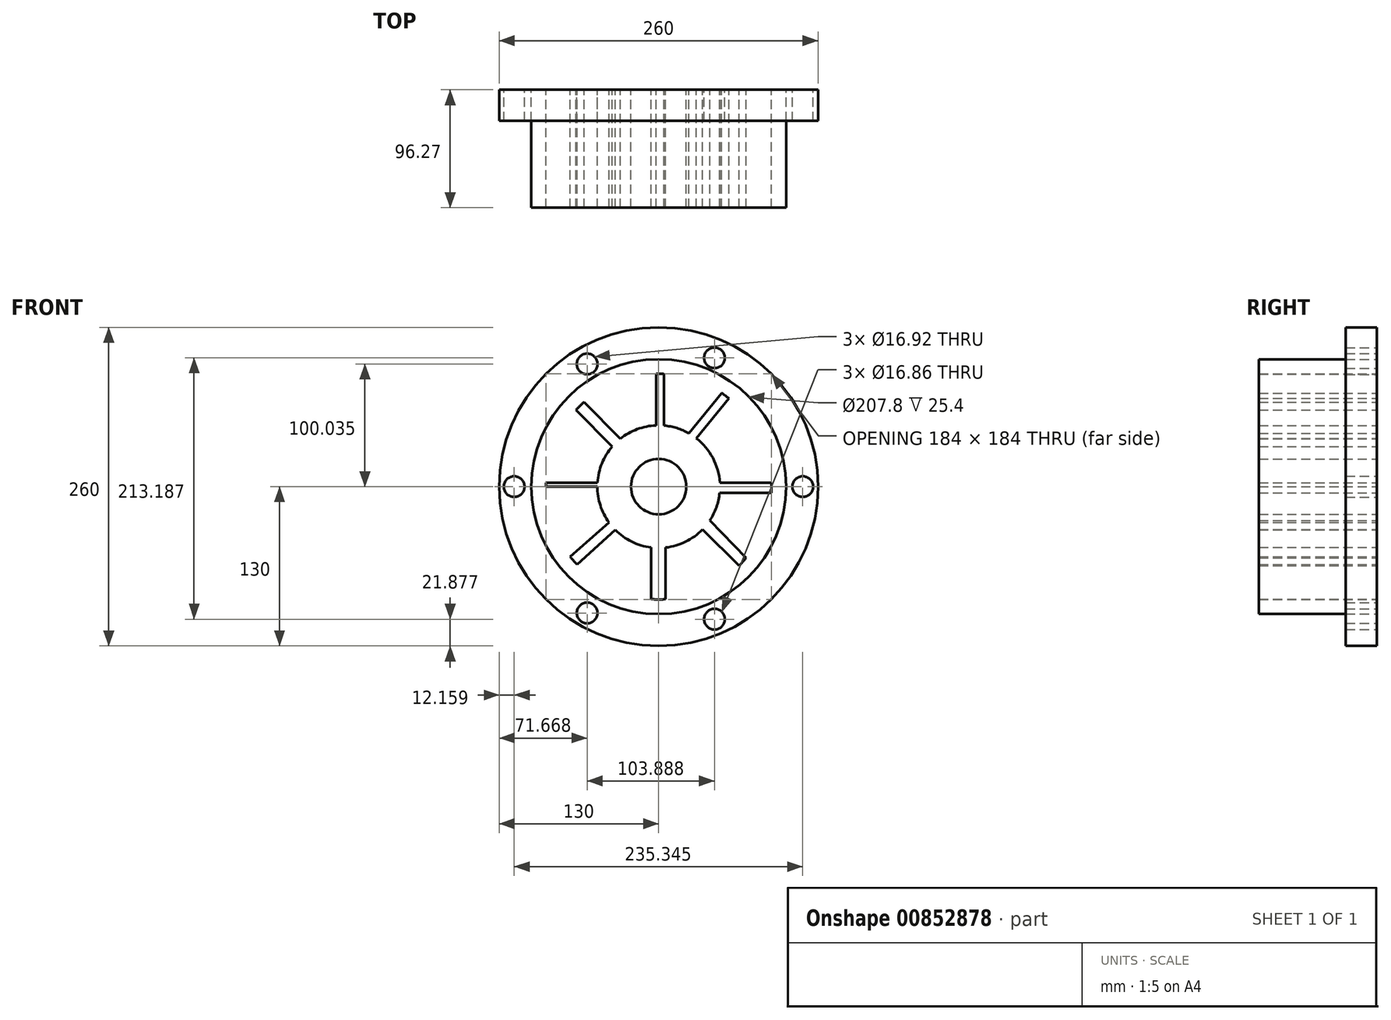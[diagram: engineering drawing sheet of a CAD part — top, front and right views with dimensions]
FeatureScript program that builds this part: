
annotation { "Feature Type Name" : "Feature", "Feature Type Description" : "" }
export const myFeature = defineFeature(function(context is Context, id is Id, definition is map)
    precondition{}
    {
        {
            var Q0;
            Q0=qCreatedBy(makeId("Front.planeOp"),FACE);
            var sketch = newSketch(context, id + "F0", { "sketchPlane" : qUnion([Q0])});
            skCircle(sketch, "E0", {"center": v(0, 0) * mm, "radius": 40 * mm});
            skCircle(sketch, "E1", {"center": v(0, 0) * mm, "radius": 22.57 * mm});
            skCircle(sketch, "E2", {"center": v(0, 0) * mm, "radius": 45 * mm});
            skCircle(sketch, "E3", {"center": v(0, 0) * mm, "radius": 50 * mm});
            skCircle(sketch, "E4", {"center": v(0, 0) * mm, "radius": 103.9 * mm});
            skCircle(sketch, "E5", {"center": v(0, 0) * mm, "radius": 92 * mm});
            skCircle(sketch, "E6", {"center": v(0, 0) * mm, "radius": 100 * mm});
            skCircle(sketch, "E7", {"center": v(0, 0) * mm, "radius": 130 * mm});
            skCircle(sketch, "E8", {"center": v(-117.84, 0) * mm, "radius": 8.46 * mm});
            skCircle(sketch, "E9", {"center": v(117.5, 0) * mm, "radius": 8.46 * mm});
            skCircle(sketch, "E10", {"center": v(-58.33, 100.04) * mm, "radius": 8.46 * mm});
            skCircle(sketch, "E11", {"center": v(45.56, 105.06) * mm, "radius": 8.43 * mm});
            skCircle(sketch, "E12", {"center": v(-58.33, -103.05) * mm, "radius": 8.43 * mm});
            skCircle(sketch, "E13", {"center": v(45.56, -108.12) * mm, "radius": 8.43 * mm});
            skLineSegment(sketch, "E14", {"start": v(2.97, -49.91) * mm, "end": v(2.97, -91.95) * mm});
            skLineSegment(sketch, "E15", {"start": v(-4.36, -49.8) * mm, "end": v(-4.36, -91.9) * mm});
            skLineSegment(sketch, "E16", {"start": v(-6.18, -49.62) * mm, "end": v(-6.18, -91.8) * mm});
            skLineSegment(sketch, "E17", {"start": v(5.65, -49.68) * mm, "end": v(5.65, -91.83) * mm});
            skLineSegment(sketch, "E18", {"start": v(-36.4, -34.28) * mm, "end": v(-67.47, -62.54) * mm});
            skLineSegment(sketch, "E19", {"start": v(-71.39, -58.03) * mm, "end": v(-39.83, -30.23) * mm});
            skLineSegment(sketch, "E20", {"start": v(-40.57, -29.23) * mm, "end": v(-72.16, -57.07) * mm});
            skLineSegment(sketch, "E21", {"start": v(-66.45, -63.62) * mm, "end": v(-35.36, -35.35) * mm});
            skLineSegment(sketch, "E22", {"start": v(-49.98, 1.43) * mm, "end": v(-91.99, 1.43) * mm});
            skLineSegment(sketch, "E23", {"start": v(-50, 0) * mm, "end": v(-92, 0) * mm});
            skLineSegment(sketch, "E24", {"start": v(-91.99, -1.6) * mm, "end": v(-50, -1.6) * mm});
            skLineSegment(sketch, "E25", {"start": v(-91.94, 3.26) * mm, "end": v(-49.9, 3.26) * mm});
            skLineSegment(sketch, "E26.MirrorCS", {"start": v(-91.99, 1.6) * mm, "end": v(-50, 1.6) * mm});
            skLineSegment(sketch, "E27", {"start": v(2.03, 49.96) * mm, "end": v(2.03, 91.98) * mm});
            skLineSegment(sketch, "E28", {"start": v(0, 92) * mm, "end": v(0, 49.96) * mm});
            skLineSegment(sketch, "E29", {"start": v(-2.07, 91.98) * mm, "end": v(-2.07, 49.96) * mm});
            skLineSegment(sketch, "E30", {"start": v(4.32, 91.9) * mm, "end": v(4.32, 49.81) * mm});
            skLineSegment(sketch, "E31", {"start": v(28.76, 40.9) * mm, "end": v(55.54, 73.34) * mm});
            skLineSegment(sketch, "E32", {"start": v(53.79, 74.64) * mm, "end": v(27.07, 42.04) * mm});
            skLineSegment(sketch, "E33", {"start": v(57.35, 71.94) * mm, "end": v(30.72, 39.45) * mm});
            skLineSegment(sketch, "E34", {"start": v(51.4, 76.3) * mm, "end": v(24.55, 43.56) * mm});
            skLineSegment(sketch, "E35", {"start": v(-33.6, 37.03) * mm, "end": v(-63.15, 66.9) * mm});
            skLineSegment(sketch, "E36", {"start": v(-65.36, 64.75) * mm, "end": v(-35.65, 35.06) * mm});
            skLineSegment(sketch, "E37", {"start": v(-67.54, 62.47) * mm, "end": v(-37.79, 32.74) * mm});
            skLineSegment(sketch, "E38", {"start": v(-60.8, 69.04) * mm, "end": v(-31.18, 39.1) * mm});
            skLineSegment(sketch, "E39", {"start": v(50, 0) * mm, "end": v(92, 0) * mm});
            skLineSegment(sketch, "E40", {"start": v(49.96, -2) * mm, "end": v(91.98, -2) * mm});
            skLineSegment(sketch, "E41", {"start": v(49.9, 3.22) * mm, "end": v(91.94, 3.22) * mm});
            skLineSegment(sketch, "E42", {"start": v(49.74, -5.08) * mm, "end": v(91.86, -5.08) * mm});
            skLineSegment(sketch, "E43", {"start": v(37.83, -32.7) * mm, "end": v(67.58, -62.42) * mm});
            skLineSegment(sketch, "E44", {"start": v(39.6, -30.54) * mm, "end": v(69.39, -60.4) * mm});
            skLineSegment(sketch, "E45", {"start": v(41.7, -27.58) * mm, "end": v(71.39, -58.03) * mm});
            skLineSegment(sketch, "E46", {"start": v(35.79, -34.92) * mm, "end": v(65.6, -64.5) * mm});
            skSolve(sketch);
        }
        {
            var Q0;
            Q0=makeQuery(id+"F0.imprint","IMPRINT",FACE,{"disambiguationData":[TD([[makeQuery(id+"F0.imprint","IMPRINT",EDGE,{"derivedFrom":sQuery(id+"F0.wireOp",EDGE,"E4")}),-1.0]])]});
            extrude(context, id + "F1", {"entities" : qUnion([Q0]), "depth" : 25.4 * mm, "offsetDistance" : 25.4 * mm});
        }
        {
            var Q0;
            Q0=makeQuery(id+"F0.imprint","IMPRINT",FACE,{"disambiguationData":[TD([[makeQuery(id+"F0.imprint","IMPRINT",EDGE,{"derivedFrom":sQuery(id+"F0.wireOp",EDGE,"E1")}),1.0]])]});
            var Q1;
            {var subQ0=sQuery(id+"F0.wireOp",EDGE,"E29");Q1=makeQuery(id+"F0.imprint","IMPRINT",FACE,{"disambiguationData":[TD([[makeQuery(id+"F0.imprint","IMPRINT",EDGE,{"derivedFrom":subQ0}),-1.0]])]});}
            var Q2;
            {var subQ0=sQuery(id+"F0.wireOp",EDGE,"E30");Q2=makeQuery(id+"F0.imprint","IMPRINT",FACE,{"disambiguationData":[TD([[makeQuery(id+"F0.imprint","IMPRINT",EDGE,{"derivedFrom":subQ0}),1.0]])]});}
            var Q3;
            {var subQ0=sQuery(id+"F0.wireOp",EDGE,"E33");Q3=makeQuery(id+"F0.imprint","IMPRINT",FACE,{"disambiguationData":[TD([[makeQuery(id+"F0.imprint","IMPRINT",EDGE,{"derivedFrom":subQ0}),1.0]])]});}
            var Q4;
            {var subQ0=sQuery(id+"F0.wireOp",EDGE,"E42");Q4=makeQuery(id+"F0.imprint","IMPRINT",FACE,{"disambiguationData":[TD([[makeQuery(id+"F0.imprint","IMPRINT",EDGE,{"derivedFrom":subQ0}),-1.0]])]});}
            var Q5;
            {var subQ0=sQuery(id+"F0.wireOp",EDGE,"E17");Q5=makeQuery(id+"F0.imprint","IMPRINT",FACE,{"disambiguationData":[TD([[makeQuery(id+"F0.imprint","IMPRINT",EDGE,{"derivedFrom":subQ0}),1.0]])]});}
            var Q6;
            {var subQ0=sQuery(id+"F0.wireOp",EDGE,"E16");Q6=makeQuery(id+"F0.imprint","IMPRINT",FACE,{"disambiguationData":[TD([[makeQuery(id+"F0.imprint","IMPRINT",EDGE,{"derivedFrom":subQ0}),-1.0]])]});}
            var Q7;
            {var subQ0=sQuery(id+"F0.wireOp",EDGE,"E20");Q7=makeQuery(id+"F0.imprint","IMPRINT",FACE,{"disambiguationData":[TD([[makeQuery(id+"F0.imprint","IMPRINT",EDGE,{"derivedFrom":subQ0}),-1.0]])]});}
            var Q8;
            {var subQ0=sQuery(id+"F0.wireOp",EDGE,"E25");Q8=makeQuery(id+"F0.imprint","IMPRINT",FACE,{"disambiguationData":[TD([[makeQuery(id+"F0.imprint","IMPRINT",EDGE,{"derivedFrom":subQ0}),1.0]])]});}
            var Q9;
            Q9=makeQuery(id+"F0.imprint","IMPRINT",FACE,{"disambiguationData":[TD([[makeQuery(id+"F0.imprint","IMPRINT",EDGE,{"derivedFrom":sQuery(id+"F0.wireOp",EDGE,"E6")}),1.0]])]});
            var Q10;
            Q10=makeQuery(id+"F0.imprint","IMPRINT",FACE,{"disambiguationData":[TD([[makeQuery(id+"F0.imprint","IMPRINT",EDGE,{"derivedFrom":sQuery(id+"F0.wireOp",EDGE,"E6")}),-1.0]])]});
            extrude(context, id + "F2", {"entities" : qUnion([Q0, Q1, Q2, Q3, Q4, Q5, Q6, Q7, Q8, Q9, Q10]), "depth" : 96.27 * mm, "offsetDistance" : 25.4 * mm});
        }
    });
